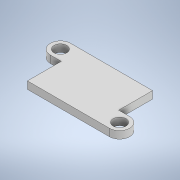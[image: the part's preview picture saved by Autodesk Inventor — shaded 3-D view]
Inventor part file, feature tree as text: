
AUTODESK INVENTOR PART (.ipt)
format: ipt  version: 2020 (Build 240168000, 168)  size: 117,248 bytes
history: native  units: in
note: dims shown in document units (in); Inventor stores cm internally (conversion verified against a paired STEP export)
features: extrude x1, sketch x1
ambient origin geometry x8: Origin, YZ Plane, XZ Plane, XY Plane, X Axis, Y Axis, Z Axis, Center Point
bodies: Solid1 (feature_tree)
feature tree (2):
  extrude  "Extrusion1"  Depth=0.0787in
  sketch  "Sketch1"  dims[d0=0.68in d1=0.5in d2=0.1378in d3=0.1378in d4=0.1575in d5=0.1575in d6=0.2165in d7=0.2165in d8=0.0787in d9=0.0in]
